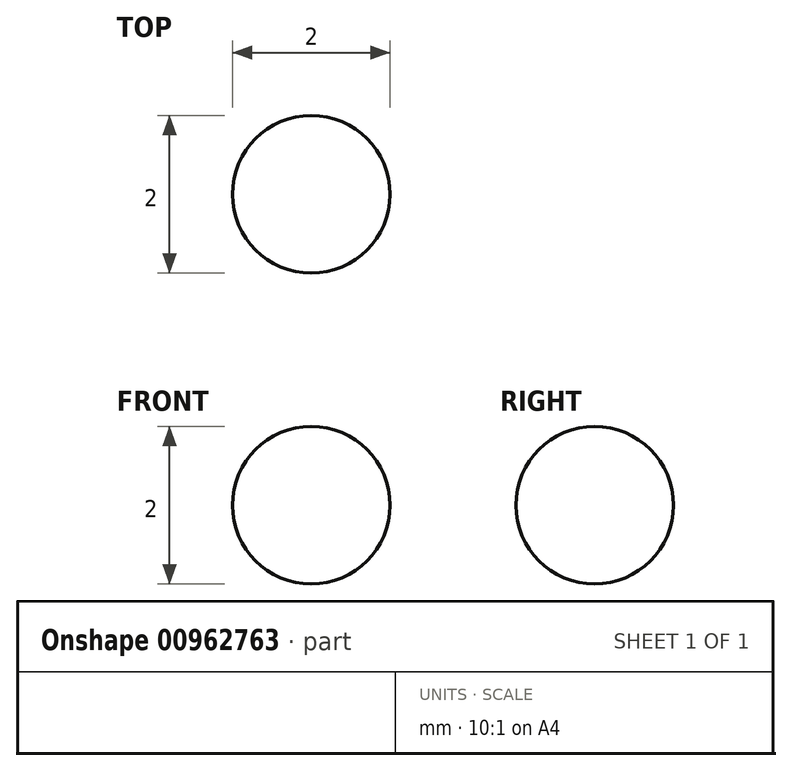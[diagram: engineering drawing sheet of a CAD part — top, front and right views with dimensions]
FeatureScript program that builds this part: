
annotation { "Feature Type Name" : "Feature", "Feature Type Description" : "" }
export const myFeature = defineFeature(function(context is Context, id is Id, definition is map)
    precondition{}
    {
        {
            var Q0;
            Q0=qCreatedBy(makeId("Top.planeOp"),FACE);
            var sketch = newSketch(context, id + "F0", { "sketchPlane" : qUnion([Q0])});
            skArc(sketch, "E0", {"start": v(6, 0) * mm, "mid": v(7, 1) * mm, "end": v(8, 0) * mm});
            skLineSegment(sketch, "E1", {"start": v(6, 0) * mm, "end": v(8, 0) * mm});
            skSolve(sketch);
        }
        {
            var Q0;
            Q0=qSketchRegion(id+"F0",true);
            var Q1;
            Q1=sQuery(id+"F0.wireOp",EDGE,"E1");
            revolve(context, id + "F1", {"surfaceOperationType" : NewSurfaceOperationType.NEW, "entities" : qUnion([Q0]), "axis" : qUnion([Q1]), "revolveType" : RevolveType.FULL});
        }
    });
